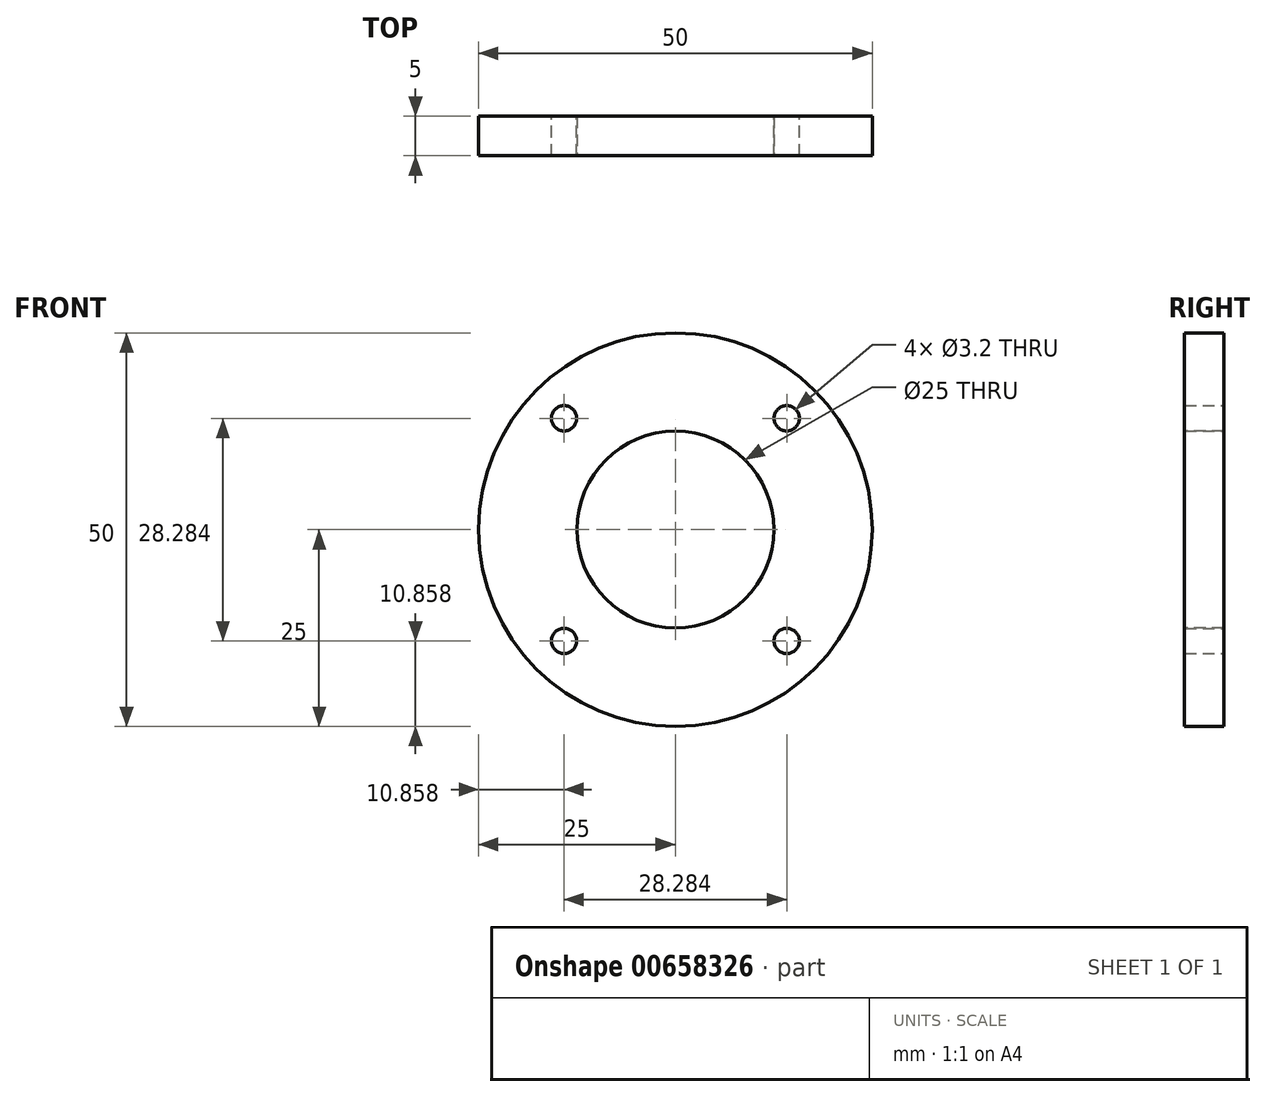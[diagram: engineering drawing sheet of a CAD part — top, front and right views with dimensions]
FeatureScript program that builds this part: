
annotation { "Feature Type Name" : "Feature", "Feature Type Description" : "" }
export const myFeature = defineFeature(function(context is Context, id is Id, definition is map)
    precondition{}
    {
        {
            var Q0;
            Q0=qCreatedBy(makeId("Front.planeOp"),FACE);
            var sketch = newSketch(context, id + "F0", { "sketchPlane" : qUnion([Q0])});
            skCircle(sketch, "E0", {"center": v(0, 0) * mm, "radius": 25 * mm});
            skCircle(sketch, "E1", {"center": v(-14.14, 14.14) * mm, "radius": 1.6 * mm});
            skCircle(sketch, "E2", {"center": v(14.14, 14.14) * mm, "radius": 1.6 * mm});
            skCircle(sketch, "E3", {"center": v(14.14, -14.14) * mm, "radius": 1.6 * mm});
            skCircle(sketch, "E4", {"center": v(-14.14, -14.14) * mm, "radius": 1.6 * mm});
            skLineSegment(sketch, "E5", {"start": v(0, 0) * mm, "end": v(-14.14, 14.14) * mm, "construction": true});
            skLineSegment(sketch, "E6", {"start": v(0, 0) * mm, "end": v(14.14, 14.14) * mm, "construction": true});
            skLineSegment(sketch, "E7", {"start": v(0, 0) * mm, "end": v(14.14, -14.14) * mm, "construction": true});
            skLineSegment(sketch, "E8", {"start": v(0, 0) * mm, "end": v(-14.14, -14.14) * mm, "construction": true});
            skSolve(sketch);
        }
        {
            var Q0;
            Q0=makeQuery(id+"F0.imprint","IMPRINT",FACE,{"disambiguationData":[TD([[makeQuery(id+"F0.imprint","IMPRINT",EDGE,{"derivedFrom":sQuery(id+"F0.wireOp",EDGE,"E0")}),1.0]])]});
            extrude(context, id + "F1", {"entities" : qUnion([Q0]), "depth" : 5 * mm, "offsetDistance" : 25 * mm});
        }
        {
            var Q0;
            Q0=makeQuery(id+"F1.opExtrude","CAP_FACE",FACE,{"disambiguationData":[OSD([sQuery(id+"F0.wireOp",EDGE,"E0"),sQuery(id+"F0.wireOp",EDGE,"E1"),sQuery(id+"F0.wireOp",EDGE,"E2"),sQuery(id+"F0.wireOp",EDGE,"E3"),sQuery(id+"F0.wireOp",EDGE,"E4")])],"isStart":false});
            var sketch = newSketch(context, id + "F2", { "sketchPlane" : qUnion([Q0])});
            skCircle(sketch, "E9", {"center": v(0, 0) * mm, "radius": 12.5 * mm});
            skSolve(sketch);
        }
        {
            var Q0;
            Q0=makeQuery(id+"F2.imprint","IMPRINT",FACE,{"disambiguationData":[TD([[makeQuery(id+"F2.imprint","IMPRINT",EDGE,{"derivedFrom":sQuery(id+"F2.wireOp",EDGE,"E9")}),1.0]])]});
            extrude(context, id + "F3", {"entities" : qUnion([Q0]), "operationType" : NewBodyOperationType.REMOVE, "oppositeDirection" : true, "depth" : 51.2 * mm, "offsetDistance" : 25 * mm});
        }
    });
